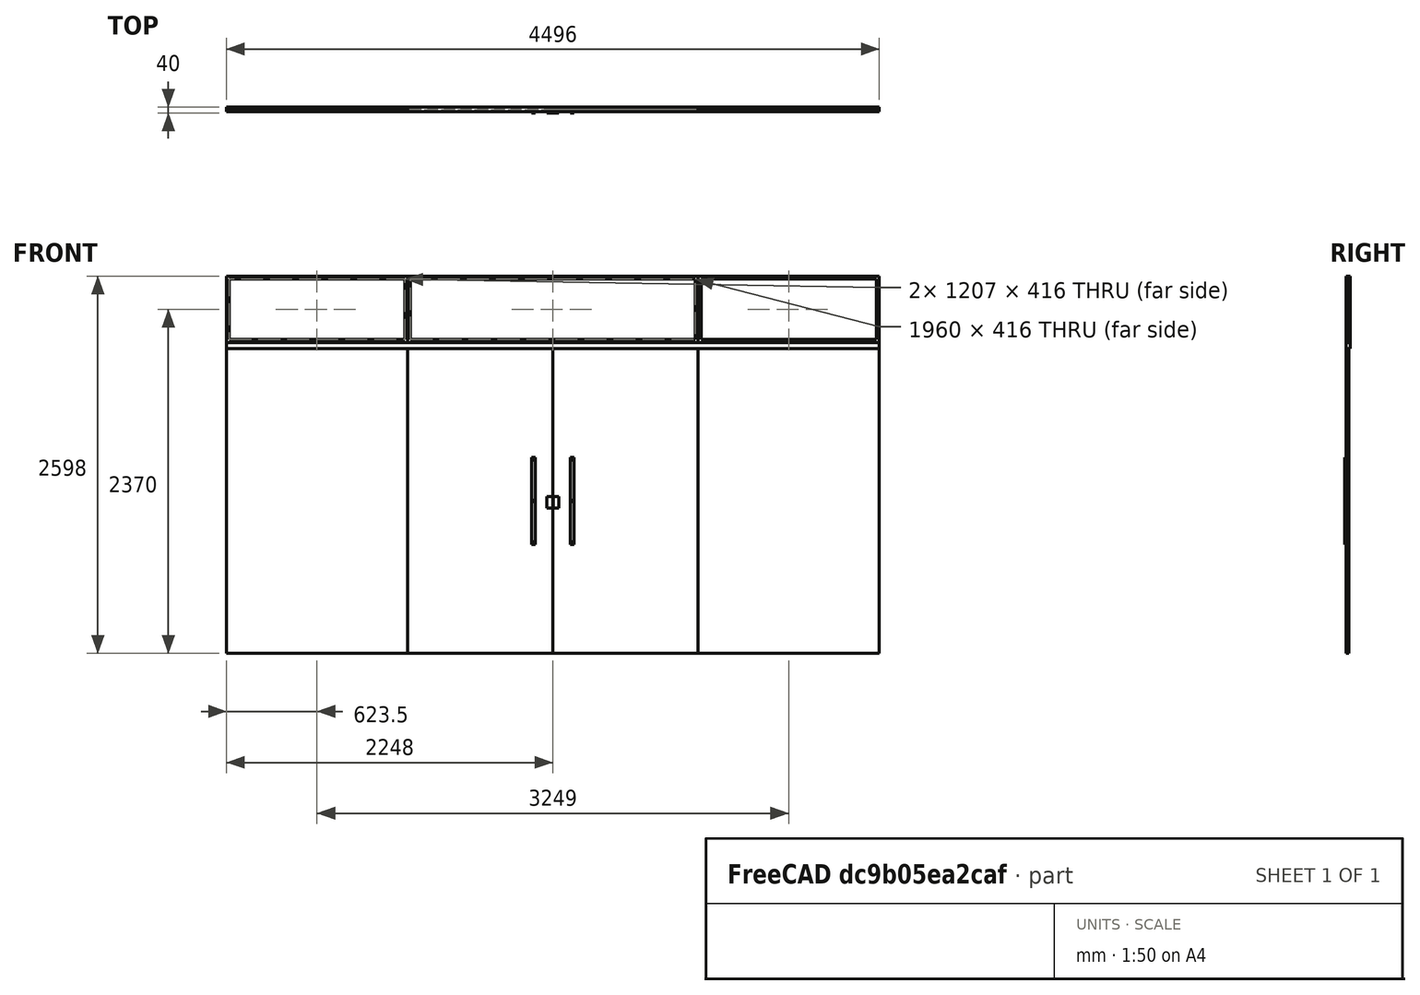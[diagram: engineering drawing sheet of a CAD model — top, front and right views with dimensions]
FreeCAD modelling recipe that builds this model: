
FCSTD DOCUMENT  (FreeCAD 0.16R6704 (Git))
Label: Double glass sliding doors and handles
License: CreativeCommons Attribution
LicenseURL: http://creativecommons.org/licenses/by/4.0/
objects: Sketcher::SketchObject×1, Part::FeaturePython×1
note: 2 computed .brp shape members not serialized (recipe doc carries the construction recipe); baked Part::Feature solids carry a one-line shape summary decoded from their .brp

FEATURE [Sketcher::SketchObject] Sketch141
  Placement = pos=(0,0,0) rot=(1,0,0;1.5708rad)
  sketch-geometry (95):
    g0: LineSegment StartX=1 StartY=0 StartZ=0 EndX=4499 EndY=0 EndZ=0
    g1: LineSegment StartX=4499 StartY=0 StartZ=0 EndX=4499 EndY=2599 EndZ=0
    g2: LineSegment StartX=4499 StartY=2599 StartZ=0 EndX=1 EndY=2599 EndZ=0
    g3: LineSegment StartX=1 StartY=2599 StartZ=0 EndX=1 EndY=0 EndZ=0
    g4: LineSegment StartX=1250 StartY=0 StartZ=0 EndX=2249.5 EndY=0 EndZ=0
    g5: LineSegment StartX=2249.5 StartY=0 StartZ=0 EndX=2249.5 EndY=2100 EndZ=0
    g6: LineSegment StartX=2249.5 StartY=2100 StartZ=0 EndX=1250 EndY=2100 EndZ=0
    g7: LineSegment StartX=1250 StartY=2100 StartZ=0 EndX=1250 EndY=0 EndZ=0
    g8: LineSegment StartX=1251 StartY=2099 StartZ=0 EndX=1351 EndY=2099 EndZ=0
    g9: LineSegment StartX=1351 StartY=2099 StartZ=0 EndX=1351 EndY=2069 EndZ=0
    g10: LineSegment StartX=1351 StartY=2069 StartZ=0 EndX=1251 EndY=2069 EndZ=0
    g11: LineSegment StartX=1251 StartY=2069 StartZ=0 EndX=1251 EndY=2099 EndZ=0
    g12: LineSegment StartX=1251 StartY=1 StartZ=0 EndX=1351 EndY=1 EndZ=0
    g13: LineSegment StartX=1351 StartY=1 StartZ=0 EndX=1351 EndY=31 EndZ=0
    g14: LineSegment StartX=1351 StartY=31 StartZ=0 EndX=1251 EndY=31 EndZ=0
    g15: LineSegment StartX=1251 StartY=31 StartZ=0 EndX=1251 EndY=1 EndZ=0
    g16: LineSegment StartX=2208.5 StartY=1080 StartZ=0 EndX=2248.5 EndY=1080 EndZ=0
    g17: LineSegment StartX=2248.5 StartY=1080 StartZ=0 EndX=2248.5 EndY=1000 EndZ=0
    g18: LineSegment StartX=2248.5 StartY=1000 StartZ=0 EndX=2208.5 EndY=1000 EndZ=0
    g19: LineSegment StartX=2208.5 StartY=1000 StartZ=0 EndX=2208.5 EndY=1080 EndZ=0
    g20: LineSegment StartX=2104.5 StartY=1350 StartZ=0 EndX=2129.5 EndY=1350 EndZ=0
    g21: LineSegment StartX=2129.5 StartY=1350 StartZ=0 EndX=2129.5 EndY=750 EndZ=0
    g22: LineSegment StartX=2129.5 StartY=750 StartZ=0 EndX=2104.5 EndY=750 EndZ=0
    g23: LineSegment StartX=2104.5 StartY=750 StartZ=0 EndX=2104.5 EndY=1350 EndZ=0
    g24: LineSegment [constr] StartX=2117 StartY=1477.64 StartZ=0 EndX=2117 EndY=711 EndZ=0
    g25: Circle CenterX=2117 CenterY=1335 CenterZ=0 NormalX=0 NormalY=0 NormalZ=1 Radius=5
    g26: Circle CenterX=2117 CenterY=1050 CenterZ=0 NormalX=0 NormalY=0 NormalZ=1 Radius=5
    g27: Circle CenterX=2117 CenterY=765 CenterZ=0 NormalX=0 NormalY=0 NormalZ=1 Radius=5
    g28: LineSegment [constr] StartX=712 StartY=1050 StartZ=0 EndX=790 EndY=1050 EndZ=0
    g29: LineSegment StartX=3250 StartY=0 StartZ=0 EndX=2250.5 EndY=0 EndZ=0
    g30: LineSegment StartX=2250.5 StartY=0 StartZ=0 EndX=2250.5 EndY=2100 EndZ=0
    g31: LineSegment StartX=2250.5 StartY=2100 StartZ=0 EndX=3250 EndY=2100 EndZ=0
    g32: LineSegment StartX=3250 StartY=2100 StartZ=0 EndX=3250 EndY=0 EndZ=0
    g33: LineSegment StartX=3249 StartY=2099 StartZ=0 EndX=1961.24 EndY=2099 EndZ=0
    g34: LineSegment StartX=1961.24 StartY=2099 StartZ=0 EndX=1961.24 EndY=2069.17 EndZ=0
    g35: LineSegment StartX=1961.24 StartY=2069.17 StartZ=0 EndX=3249 EndY=2069.17 EndZ=0
    g36: LineSegment StartX=3249 StartY=2069.17 StartZ=0 EndX=3249 EndY=2099 EndZ=0
    g37: LineSegment StartX=3249 StartY=1 StartZ=0 EndX=1961.24 EndY=1 EndZ=0
    g38: LineSegment StartX=1961.24 StartY=1 StartZ=0 EndX=1961.24 EndY=30.8302 EndZ=0
    g39: LineSegment StartX=1961.24 StartY=30.8302 StartZ=0 EndX=3249 EndY=30.8302 EndZ=0
    g40: LineSegment StartX=3249 StartY=30.8302 StartZ=0 EndX=3249 EndY=1 EndZ=0
    g41: LineSegment StartX=2251.5 StartY=1080 StartZ=0 EndX=2291.5 EndY=1080 EndZ=0
    g42: LineSegment StartX=2291.5 StartY=1080 StartZ=0 EndX=2291.5 EndY=1000 EndZ=0
    g43: LineSegment StartX=2291.5 StartY=1000 StartZ=0 EndX=2251.5 EndY=1000 EndZ=0
    g44: LineSegment StartX=2251.5 StartY=1000 StartZ=0 EndX=2251.5 EndY=1080 EndZ=0
    g45: LineSegment StartX=2370.5 StartY=1350 StartZ=0 EndX=2395.5 EndY=1350 EndZ=0
    g46: LineSegment StartX=2395.5 StartY=1350 StartZ=0 EndX=2395.5 EndY=750 EndZ=0
    g47: LineSegment StartX=2395.5 StartY=750 StartZ=0 EndX=2370.5 EndY=750 EndZ=0
    g48: LineSegment StartX=2370.5 StartY=750 StartZ=0 EndX=2370.5 EndY=1350 EndZ=0
    g49: LineSegment [constr] StartX=2383 StartY=1477.64 StartZ=0 EndX=2383 EndY=711 EndZ=0
    g50: Circle CenterX=2383 CenterY=1335 CenterZ=0 NormalX=0 NormalY=0 NormalZ=1 Radius=5
    g51: Circle CenterX=2383 CenterY=1050 CenterZ=0 NormalX=0 NormalY=0 NormalZ=1 Radius=5
    g52: Circle CenterX=2383 CenterY=765 CenterZ=0 NormalX=0 NormalY=0 NormalZ=1 Radius=5
    g53: LineSegment [constr] StartX=1088 StartY=1050 StartZ=0 EndX=1010 EndY=1050 EndZ=0
    g54: LineSegment StartX=0 StartY=2600 StartZ=0 EndX=4500 EndY=2600 EndZ=0
    g55: LineSegment StartX=4500 StartY=2600 StartZ=0 EndX=4500 EndY=0 EndZ=0
    g56: LineSegment StartX=4500 StartY=0 StartZ=0 EndX=0 EndY=0 EndZ=0
    g57: LineSegment StartX=0 StartY=0 StartZ=0 EndX=0 EndY=2600 EndZ=0
    g58: LineSegment StartX=1250 StartY=2598 StartZ=0 EndX=3250 EndY=2598 EndZ=0
    g59: LineSegment StartX=3250 StartY=2598 StartZ=0 EndX=3250 EndY=2142 EndZ=0
    g60: LineSegment StartX=3250 StartY=2142 StartZ=0 EndX=1250 EndY=2142 EndZ=0
    g61: LineSegment StartX=1250 StartY=2142 StartZ=0 EndX=1250 EndY=2598 EndZ=0
    g62: LineSegment StartX=1270 StartY=2578 StartZ=0 EndX=3230 EndY=2578 EndZ=0
    g63: LineSegment StartX=3230 StartY=2578 StartZ=0 EndX=3230 EndY=2162 EndZ=0
    g64: LineSegment StartX=3230 StartY=2162 StartZ=0 EndX=1270 EndY=2162 EndZ=0
    g65: LineSegment StartX=1270 StartY=2162 StartZ=0 EndX=1270 EndY=2578 EndZ=0
    g66: LineSegment StartX=2 StartY=2141 StartZ=0 EndX=4498 EndY=2141 EndZ=0
    g67: LineSegment StartX=4498 StartY=2141 StartZ=0 EndX=4498 EndY=2101 EndZ=0
    g68: LineSegment StartX=4498 StartY=2101 StartZ=0 EndX=2 EndY=2101 EndZ=0
    g69: LineSegment StartX=2 StartY=2101 StartZ=0 EndX=2 EndY=2141 EndZ=0
    g70: LineSegment [constr] StartX=2250 StartY=3422 StartZ=0 EndX=2250 EndY=-753 EndZ=0
    g71: LineSegment StartX=2 StartY=2598 StartZ=0 EndX=1249 EndY=2598 EndZ=0
    g72: LineSegment StartX=1249 StartY=2598 StartZ=0 EndX=1249 EndY=2142 EndZ=0
    g73: LineSegment StartX=1249 StartY=2142 StartZ=0 EndX=2 EndY=2142 EndZ=0
    g74: LineSegment StartX=2 StartY=2142 StartZ=0 EndX=2 EndY=2598 EndZ=0
    g75: LineSegment StartX=22 StartY=2578 StartZ=0 EndX=1229 EndY=2578 EndZ=0
    g76: LineSegment StartX=1229 StartY=2578 StartZ=0 EndX=1229 EndY=2162 EndZ=0
    g77: LineSegment StartX=1229 StartY=2162 StartZ=0 EndX=22 EndY=2162 EndZ=0
    g78: LineSegment StartX=22 StartY=2162 StartZ=0 EndX=22 EndY=2578 EndZ=0
    g79: LineSegment StartX=3251 StartY=2598 StartZ=0 EndX=4498 EndY=2598 EndZ=0
    g80: LineSegment StartX=4498 StartY=2598 StartZ=0 EndX=4498 EndY=2142 EndZ=0
    g81: LineSegment StartX=4498 StartY=2142 StartZ=0 EndX=3251 EndY=2142 EndZ=0
    g82: LineSegment StartX=3251 StartY=2142 StartZ=0 EndX=3251 EndY=2598 EndZ=0
    g83: LineSegment StartX=3271 StartY=2578 StartZ=0 EndX=4478 EndY=2578 EndZ=0
    g84: LineSegment StartX=4478 StartY=2578 StartZ=0 EndX=4478 EndY=2162 EndZ=0
    g85: LineSegment StartX=4478 StartY=2162 StartZ=0 EndX=3271 EndY=2162 EndZ=0
    g86: LineSegment StartX=3271 StartY=2162 StartZ=0 EndX=3271 EndY=2578 EndZ=0
    g87: LineSegment StartX=2 StartY=2100 StartZ=0 EndX=1249 EndY=2100 EndZ=0
    g88: LineSegment StartX=1249 StartY=2100 StartZ=0 EndX=1249 EndY=0 EndZ=0
    g89: LineSegment StartX=1249 StartY=0 StartZ=0 EndX=2 EndY=0 EndZ=0
    g90: LineSegment StartX=2 StartY=0 StartZ=0 EndX=2 EndY=2100 EndZ=0
    g91: LineSegment StartX=3251 StartY=2100 StartZ=0 EndX=4498 EndY=2100 EndZ=0
    g92: LineSegment StartX=4498 StartY=2100 StartZ=0 EndX=4498 EndY=0 EndZ=0
    g93: LineSegment StartX=4498 StartY=0 StartZ=0 EndX=3251 EndY=0 EndZ=0
    g94: LineSegment StartX=3251 StartY=0 StartZ=0 EndX=3251 EndY=2100 EndZ=0
  constraints (274):
    c: Coincident(g0,g1)
    c: Coincident(g1,g2)
    c: Horizontal(g0)
    c: Horizontal(g2)
    c: Vertical(g1)
    c: Coincident(g4,g5)
    c: Coincident(g5,g6)
    c: Coincident(g6,g7)
    c: Coincident(g7,g4)
    c: Horizontal(g4)
    c: Horizontal(g6)
    c: Vertical(g5)
    c: Vertical(g7)
    c: DistanceY(g0,g4) = 0  'Constraint17'
    c: Coincident(g8,g9)  'Constraint15'
    c: Coincident(g9,g10)
    c: Coincident(g10,g11)
    c: Coincident(g11,g8)
    c: Horizontal(g8)
    c: Horizontal(g10)
    c: Vertical(g9)
    c: Vertical(g11)
    c: Coincident(g12,g13)
    c: Coincident(g13,g14)
    c: Coincident(g14,g15)
    c: Coincident(g15,g12)
    c: Horizontal(g12)
    c: Horizontal(g14)
    c: Vertical(g13)
    c: Vertical(g15)
    c: Coincident(g16,g17)
    c: Coincident(g17,g18)
    c: Coincident(g18,g19)
    c: Coincident(g19,g16)
    c: Horizontal(g16)
    c: Horizontal(g18)
    c: Vertical(g17)
    c: Vertical(g19)
    c: DistanceY(g8,g6) = 1
    c: DistanceX(g6,g8) = 1
    c: DistanceY(g9,g8) = 30  'Altura do apoio'
    c: DistanceX(g10,g9) = 100  'Largura do apoio'
    c: Equal(g9,g13)
    c: Equal(g14,g8)
    c: DistanceX(g4,g12) = 1
    c: DistanceY(g4,g12) = 1
    c: DistanceX(g17,g4) = 1
    c: DistanceY(g18,g16) = 80  'Altura da tranca'
    c: DistanceX(g16,g16) = 40  'Largura da tranca'
    c: DistanceY(g4,g18) = 1000  'Altura da tranca ao chão'
    c: Coincident(g20,g21)
    c: Coincident(g21,g22)
    c: Coincident(g22,g23)
    c: Coincident(g23,g20)
    c: Horizontal(g20)
    c: Horizontal(g22)
    c: Vertical(g21)
    c: Vertical(g23)
    c: DistanceX(g20,g20) = 25  'Largura puxador'
    c: DistanceY(g21,g20) = 600  'Altura do puxdor'
    c: Vertical(g24)  'Constraint69'
    c: Symmetric(g20,g20,g24)  'Constraint67'
    c: PointOnObject(g25,g24)  'Constraint72'
    c: PointOnObject(g26,g24)  'Constraint71'
    c: PointOnObject(g27,g24)  'Constraint68'
    c: Radius(g27) = 5  'Apoio puxador'
    c: Equal(g27,g26)  'Constraint83'
    c: Equal(g27,g25)  'Constraint82'
    c: DistanceY(g25,g20) = 15  'Constraint70'
    c: DistanceY(g21,g27) = 15
    c: Horizontal(g28)
    c: PointOnObject(g26,g28)
    c: Symmetric(g22,g20,g28)
    c: DistanceY(g4,g21) = 750  'Distância do puxador ao solo'
    c: DistanceX(g21,g4) = 120  'Distância do puxador'
    c: Coincident(g29,g30)
    c: Coincident(g30,g31)
    c: Coincident(g31,g32)
    c: Coincident(g32,g29)
    c: Horizontal(g29)
    c: Horizontal(g31)
    c: Vertical(g30)
    c: Vertical(g32)
    c: Coincident(g33,g34)
    c: Coincident(g34,g35)
    c: Coincident(g35,g36)
    c: Coincident(g36,g33)
    c: Horizontal(g33)
    c: Horizontal(g35)
    c: Vertical(g34)
    c: Vertical(g36)
    c: Coincident(g37,g38)
    c: Coincident(g38,g39)
    c: Coincident(g39,g40)
    c: Coincident(g40,g37)
    c: Horizontal(g37)
    c: Horizontal(g39)
    c: Vertical(g38)
    c: Vertical(g40)
    c: Coincident(g41,g42)
    c: Coincident(g42,g43)
    c: Coincident(g43,g44)
    c: Coincident(g44,g41)
    c: Horizontal(g41)
    c: Horizontal(g43)
    c: Vertical(g42)
    c: Vertical(g44)
    c: Equal(g34,g38)
    c: Equal(g39,g33)
    c: Coincident(g45,g46)
    c: Coincident(g46,g47)
    c: Coincident(g47,g48)
    c: Coincident(g48,g45)
    c: Horizontal(g45)
    c: Horizontal(g47)
    c: Vertical(g46)
    c: Vertical(g48)
    c: Vertical(g49)  'Constraint69'
    c: Symmetric(g45,g45,g49)
    c: PointOnObject(g50,g49)  'Constraint72'
    c: PointOnObject(g51,g49)
    c: PointOnObject(g52,g49)  'Constraint127'
    c: Radius(g52) = 5  'Apoio puxador'
    c: Equal(g52,g51)  'Constraint83'
    c: Equal(g52,g50)  'Constraint82'
    c: Horizontal(g53)
    c: PointOnObject(g51,g53)
    c: Symmetric(g47,g45,g53)
    c: Coincident(g54,g55)
    c: Coincident(g55,g56)
    c: Coincident(g56,g57)
    c: Coincident(g57,g54)
    c: Horizontal(g54)
    c: Horizontal(g56)
    c: Vertical(g55)
    c: Vertical(g57)
    c: DistanceX(g54,g2) = 1
    c: DistanceY(g2,g54) = 1
    c: DistanceX(g1,g54) = 1
    c: DistanceY(g56,g-1) = 0
    c: DistanceY(g-1,g6) = 2100  'Altura portas'
    c: Coincident(g58,g59)
    c: Coincident(g59,g60)
    c: Coincident(g60,g61)
    c: Coincident(g61,g58)
    c: Horizontal(g58)
    c: Horizontal(g60)
    c: Vertical(g59)
    c: Vertical(g61)
    c: Coincident(g62,g63)
    c: Coincident(g63,g64)
    c: Coincident(g64,g65)
    c: Coincident(g65,g62)
    c: Horizontal(g62)
    c: Horizontal(g64)
    c: Vertical(g63)
    c: Vertical(g65)
    c: Coincident(g66,g67)
    c: Coincident(g67,g68)
    c: Coincident(g68,g69)
    c: Coincident(g69,g66)
    c: Horizontal(g66)
    c: Horizontal(g68)
    c: Vertical(g67)
    c: Vertical(g69)
    c: DistanceY(g66,g60) = 1
    c: DistanceX(g60,g64) = 20  'Largura do perfil 2'
    c: DistanceX(g62,g58) = 20  'Constraint168'
    c: DistanceY(g6,g68) = 1
    c: DistanceY(g68,g66) = 40  'Altura perfil bandeira'
    c: DistanceY(g58,g2) = 1  'Constraint184'
    c: DistanceY(g6,g54) = 500  'Altura bandeira'
    c: Vertical(g3)  'Constraint179'
    c: Coincident(g2,g3)  'Constraint178'
    c: Vertical(g70)
    c: DistanceY(g30,g5) = 0
    c: DistanceX(g5,g30) = 1
    c: Symmetric(g5,g30,g70)
    c: Symmetric(g54,g54,g70)
    c: Equal(g6,g31)
    c: Symmetric(g24,g49,g70)
    c: DistanceY(g33,g31) = 1
    c: DistanceX(g33,g31) = 1
    c: DistanceY(g29,g37) = 1
    c: DistanceX(g37,g29) = 1
    c: DistanceX(g2,g66) = 1
    c: DistanceX(g66,g1) = 1
    c: DistanceX(g31,g59) = 0
    c: DistanceX(g60,g6) = 0
    c: Equal(g20,g45)
    c: Equal(g16,g41)
    c: Equal(g19,g44)
    c: Symmetric(g16,g41,g70)
    c: DistanceY(g16,g41) = 0
    c: Coincident(g3,g0)
    c: DistanceX(g56,g55) = 4500  'Largura do vão'
    c: Coincident(g71,g72)
    c: Coincident(g72,g73)
    c: Coincident(g73,g74)
    c: Coincident(g74,g71)
    c: Horizontal(g71)
    c: Horizontal(g73)
    c: Vertical(g72)
    c: Vertical(g74)
    c: Coincident(g75,g76)
    c: Coincident(g76,g77)
    c: Coincident(g77,g78)
    c: Coincident(g78,g75)
    c: Horizontal(g75)
    c: Horizontal(g77)
    c: Vertical(g76)
    c: Vertical(g78)
    c: Coincident(g79,g80)
    c: Coincident(g80,g81)
    c: Coincident(g81,g82)
    c: Coincident(g82,g79)
    c: Horizontal(g79)
    c: Horizontal(g81)
    c: Vertical(g80)
    c: Vertical(g82)
    c: Coincident(g83,g84)
    c: Coincident(g84,g85)
    c: Coincident(g85,g86)
    c: Coincident(g86,g83)
    c: Horizontal(g83)
    c: Horizontal(g85)
    c: Vertical(g84)
    c: Vertical(g86)
    c: DistanceX(g79,g83) = 20  'Pefil bandeira'
    c: DistanceX(g83,g79) = 20  'Perfil vertical bandeira'
    c: DistanceX(g79,g1) = 1  'Constraint232'
    c: DistanceY(g79,g1) = 1
    c: DistanceX(g58,g79) = 1
    c: DistanceX(g71,g58) = 1
    c: DistanceY(g71,g58) = 0
    c: DistanceY(g60,g72) = 0
    c: DistanceX(g71,g75) = 20  'Perfil bandeira 2'
    c: DistanceY(g75,g71) = 20  'Perfil horizontal bandeira 2'
    c: DistanceY(g73,g77) = 20  'Perfil horizontal bandeira inferior'
    c: DistanceX(g75,g71) = 20  'Perfil vertical bandeira 4'
    c: DistanceX(g2,g71) = 1  'Constraint242'
    c: Coincident(g87,g88)
    c: Coincident(g88,g89)
    c: Coincident(g89,g90)
    c: Coincident(g90,g87)
    c: Horizontal(g87)
    c: Horizontal(g89)
    c: Vertical(g88)
    c: Vertical(g90)
    c: Coincident(g91,g92)
    c: Coincident(g92,g93)
    c: Coincident(g93,g94)
    c: Coincident(g94,g91)
    c: Horizontal(g91)
    c: Horizontal(g93)
    c: Vertical(g92)
    c: Vertical(g94)
    c: DistanceX(g68,g87) = 0
    c: DistanceY(g87,g68) = 1
    c: DistanceX(g88,g4) = 1
    c: DistanceY(g4,g88) = 0
    c: DistanceY(g56,g0) = 0
    c: DistanceY(g91,g31) = 0
    c: DistanceX(g31,g91) = 1
    c: DistanceX(g91,g67) = 0
    c: DistanceY(g55,g92) = 0
    c: DistanceX(g4,g29) = 2000  'Largura das portas'
    c: DistanceY(g29,g93) = 0  'Constraint268'
    c: DistanceY(g76,g64) = 0
    c: DistanceY(g75,g62) = 0
    c: DistanceY(g62,g83) = 0
    c: DistanceY(g63,g85) = 0
    c: DistanceY(g59,g81) = 0
    c: DistanceX(g56) = 0
FEATURE [Part::FeaturePython] Window097  label="Double glass sliding doors and handles "  # WARN: FeaturePython — macro-defined, semantics opaque (R4)
  Base = -> Sketch141
  Height = 2100
  HoleDepth = 0
  MoveWithHost = true
  Normal = (0,1,0)
  Preset = 6
  Role = 1
  Width = 900
  WindowParts = PORTA 1 | Glass panel | Wire1 | 10.0 | 0 | TRANCA 1 | Frame | Wire4 | 30.0 | -10.0 | PUXADOR 1A | Frame | Wire5 | 10.0 | -10.0 | PUXADOR 2A | Frame | Wire13 | 10.0 | -10.0 | APOIO SUPERIOR PUXADOR 1 | Frame | Wire6 | 30.0 | -10.0 | APOIO CENTRAL PUXADOR 1 | Frame | Wire7 | 30.0 | -10.0 | APOIO INFERIOR PUXADOR 1 | Frame | Wire8 | 30.0 | -10.0 | PORTA 2 | Glass panel | Wire9 | 10.0 | 0 | TRANCA 2 | Frame | Wire12 | 30.0 | -10.0 | APOIO SUPERIOR PUXADOR 2 | Frame | Wire14 | 30.0 | -10.0 | APOIO CENTRAL PUXADOR 2 | Frame | Wire15 | 30.0 | -10.0 | APOIO INFERIOR PUXADOR 2 | Frame | Wire16 | 30.0 | -10.0 | PUXADOR 2B | Frame | Wire13 | 10.0 | 10.0 | PERFIL BASE BANDEIRA | Frame | Wire20 | 30.0 | 0.0 | PERFIL BANDEIRA | Frame | Wire19,Wire18 | 30.0 | 0.0 | VIDRO BANDEIRA | Glass panel | Wire19 | 10.0 | 5.0 | VIDRO FIXO 1 | Glass panel | Wire25 | 10.0 | 10.0 | VIDRO FIXO 2 | Glass panel | Wire26 | 10.0 | 10.0 | BAQUETE BANDEIRA 1 | Frame | Wire22,Wire21 | 20.0 | 5.0 | BAQUETE BANDEIRA 2 | Frame | Wire24,Wire23 | 20.0 | 5.0 | VIDRO BANDEIRA 1 | Glass panel | Wire22 | 10.0 | 10.0 | VIDRO BANDEIRA 2 | Glass panel | Wire24 | 10.0 | 5.0 | PUXADOR 1B | Frame | Wire5 | 10.0 | 10.0
